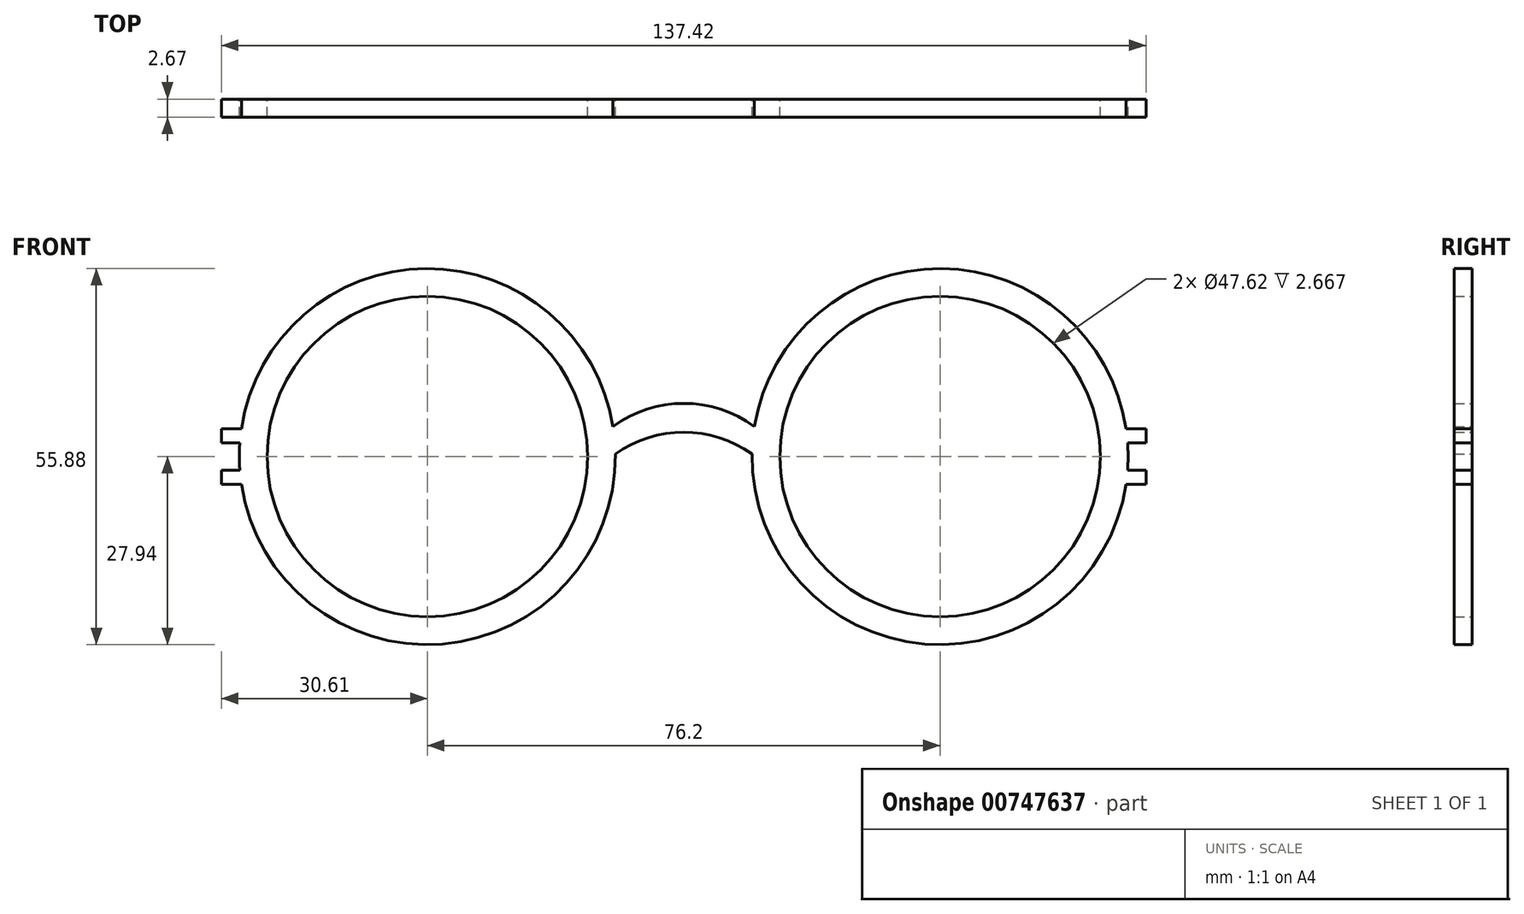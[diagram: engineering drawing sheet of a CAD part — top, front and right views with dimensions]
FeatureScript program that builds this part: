
annotation { "Feature Type Name" : "Feature", "Feature Type Description" : "" }
export const myFeature = defineFeature(function(context is Context, id is Id, definition is map)
    precondition{}
    {
        {
            var Q0;
            Q0=qCreatedBy(makeId("Front.planeOp"),FACE);
            var sketch = newSketch(context, id + "F0", { "sketchPlane" : qUnion([Q0])});
            skCircle(sketch, "E0", {"center": v(-38.1, 0) * mm, "radius": 27.94 * mm});
            skCircle(sketch, "E1", {"center": v(38.1, 0) * mm, "radius": 27.94 * mm});
            skCircle(sketch, "E2", {"center": v(-38.1, 0) * mm, "radius": 23.81 * mm});
            skCircle(sketch, "E3", {"center": v(38.1, 0) * mm, "radius": 23.81 * mm});
            skArc(sketch, "E4", {"start": v(10.52, 4.46) * mm, "mid": v(0, 7.9) * mm, "end": v(-10.52, 4.46) * mm});
            skArc(sketch, "E5", {"start": v(10.16, 0.4) * mm, "mid": v(0, 3.6) * mm, "end": v(-10.16, 0.4) * mm});
            skLineSegment(sketch, "E6.MirrorCS", {"start": v(64.06, -4.11) * mm, "end": v(68.7, -4.11) * mm});
            skLineSegment(sketch, "E7.MirrorCS", {"start": v(64.06, -2.05) * mm, "end": v(68.7, -2.05) * mm});
            skLineSegment(sketch, "E8.MirrorCS", {"start": v(68.7, -4.11) * mm, "end": v(68.7, 4.11) * mm});
            skLineSegment(sketch, "E9.MirrorCS", {"start": v(64.06, 2.05) * mm, "end": v(68.7, 2.05) * mm});
            skLineSegment(sketch, "E10.MirrorCS", {"start": v(64.06, 4.11) * mm, "end": v(68.7, 4.11) * mm});
            skLineSegment(sketch, "E11.MirrorCS", {"start": v(-64.06, 4.11) * mm, "end": v(-68.7, 4.11) * mm});
            skLineSegment(sketch, "E12.MirrorCS", {"start": v(-64.06, 2.05) * mm, "end": v(-68.7, 2.05) * mm});
            skLineSegment(sketch, "E13.MirrorCS", {"start": v(-68.7, -4.11) * mm, "end": v(-68.7, 4.11) * mm});
            skLineSegment(sketch, "E14.MirrorCS", {"start": v(-64.06, -4.11) * mm, "end": v(-68.7, -4.11) * mm});
            skLineSegment(sketch, "E15.MirrorCS", {"start": v(-64.06, -2.05) * mm, "end": v(-68.7, -2.05) * mm});
            skSolve(sketch);
        }
        {
            var Q0;
            {var subQ0=sQuery(id+"F0.wireOp",EDGE,"E11.MirrorCS");Q0=makeQuery(id+"F0.imprint","IMPRINT",FACE,{"disambiguationData":[TD([[makeQuery(id+"F0.imprint","IMPRINT",EDGE,{"derivedFrom":subQ0}),1.0]])]});}
            var Q1;
            Q1=makeQuery(id+"F0.imprint","IMPRINT",FACE,{"disambiguationData":[TD([[makeQuery(id+"F0.imprint","IMPRINT",EDGE,{"derivedFrom":sQuery(id+"F0.wireOp",EDGE,"E2")}),-1.0]])]});
            var Q2;
            {var subQ0=sQuery(id+"F0.wireOp",EDGE,"E14.MirrorCS");Q2=makeQuery(id+"F0.imprint","IMPRINT",FACE,{"disambiguationData":[TD([[makeQuery(id+"F0.imprint","IMPRINT",EDGE,{"derivedFrom":subQ0}),-1.0]])]});}
            var Q3;
            {var subQ0=sQuery(id+"F0.wireOp",EDGE,"E4");Q3=makeQuery(id+"F0.imprint","IMPRINT",FACE,{"disambiguationData":[TD([[makeQuery(id+"F0.imprint","IMPRINT",EDGE,{"derivedFrom":subQ0}),1.0]])]});}
            var Q4;
            Q4=makeQuery(id+"F0.imprint","IMPRINT",FACE,{"disambiguationData":[TD([[makeQuery(id+"F0.imprint","IMPRINT",EDGE,{"derivedFrom":sQuery(id+"F0.wireOp",EDGE,"E3")}),-1.0]])]});
            var Q5;
            {var subQ0=sQuery(id+"F0.wireOp",EDGE,"E6.MirrorCS");Q5=makeQuery(id+"F0.imprint","IMPRINT",FACE,{"disambiguationData":[TD([[makeQuery(id+"F0.imprint","IMPRINT",EDGE,{"derivedFrom":subQ0}),1.0]])]});}
            var Q6;
            {var subQ0=sQuery(id+"F0.wireOp",EDGE,"E10.MirrorCS");Q6=makeQuery(id+"F0.imprint","IMPRINT",FACE,{"disambiguationData":[TD([[makeQuery(id+"F0.imprint","IMPRINT",EDGE,{"derivedFrom":subQ0}),-1.0]])]});}
            extrude(context, id + "F1", {"entities" : qUnion([Q0, Q1, Q2, Q3, Q4, Q5, Q6]), "depth" : 2.67 * mm, "offsetDistance" : 25.4 * mm});
        }
    });
